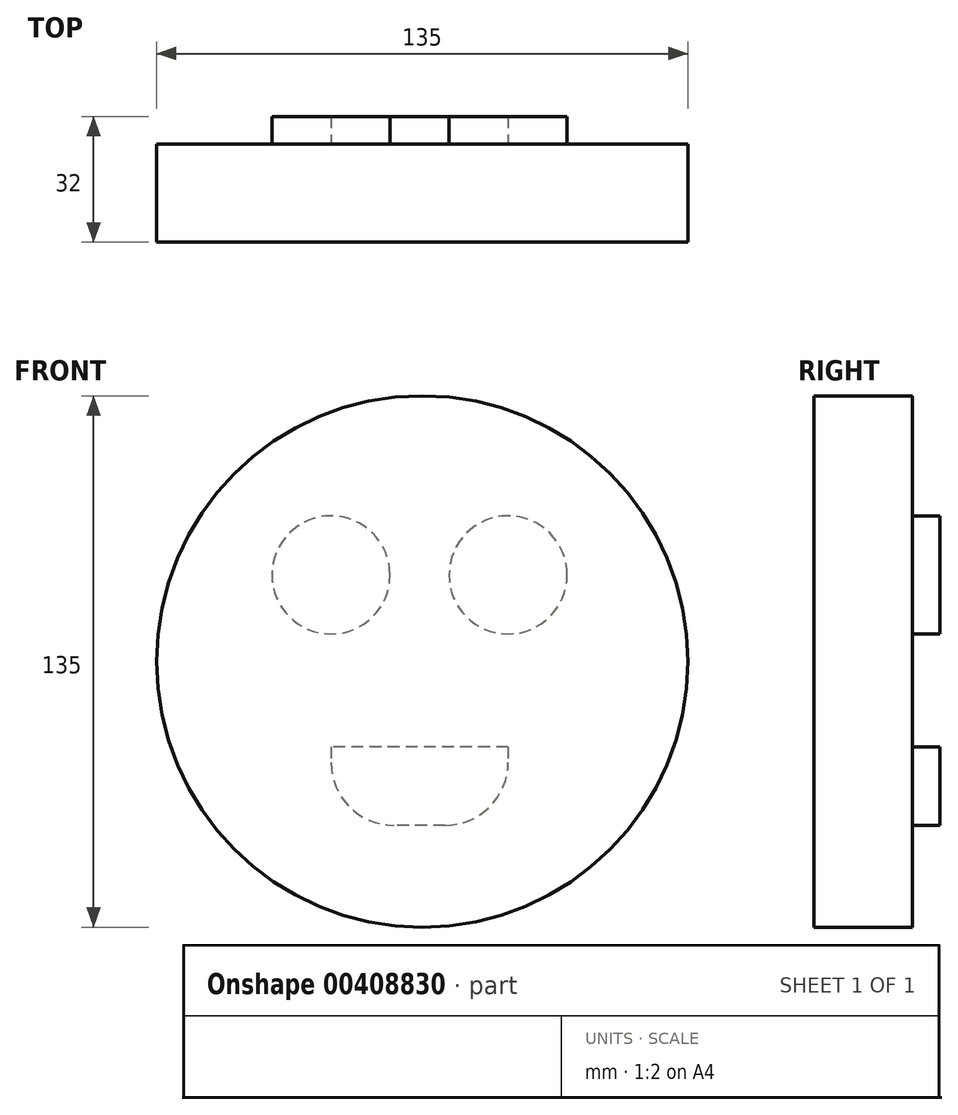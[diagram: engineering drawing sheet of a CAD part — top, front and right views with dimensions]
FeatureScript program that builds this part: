
annotation { "Feature Type Name" : "Feature", "Feature Type Description" : "" }
export const myFeature = defineFeature(function(context is Context, id is Id, definition is map)
    precondition{}
    {
        {
            var Q0;
            Q0=qCreatedBy(makeId("Front.planeOp"),FACE);
            var sketch = newSketch(context, id + "F0", { "sketchPlane" : qUnion([Q0])});
            skCircle(sketch, "E0", {"center": v(0, 0) * mm, "radius": 67.5 * mm});
            skSolve(sketch);
        }
        {
            var Q0;
            Q0 = qSketchRegion(id + "F0", true);
            extrude(context, id + "F1", {"entities" : qUnion([Q0]), "depth" : 25 * mm});
        }
        {
            var Q0;
            Q0=qCreatedBy(makeId("Front.planeOp"),FACE);
            var sketch = newSketch(context, id + "F2", { "sketchPlane" : qUnion([Q0])});
            skCircle(sketch, "E1", {"center": v(-23.18, 22) * mm, "radius": 15 * mm});
            skCircle(sketch, "E2", {"center": v(21.82, 22) * mm, "radius": 15 * mm});
            skLineSegment(sketch, "E3.bottom", {"start": v(21.82, -21.7) * mm, "end": v(-23.18, -21.7) * mm});
            skLineSegment(sketch, "E3.top", {"start": v(21.82, -41.6) * mm, "end": v(-23.18, -41.6) * mm});
            skLineSegment(sketch, "E3.left", {"start": v(21.82, -21.7) * mm, "end": v(21.82, -41.6) * mm});
            skLineSegment(sketch, "E3.right", {"start": v(-23.18, -21.7) * mm, "end": v(-23.18, -41.6) * mm});
            skSolve(sketch);
        }
        {
            var Q0;
            Q0 = qSketchRegion(id + "F2", true);
            extrude(context, id + "F3", {"entities" : qUnion([Q0]), "operationType" : NewBodyOperationType.ADD, "oppositeDirection" : true, "depth" : 7 * mm});
        }
        {
            var Q0;
            Q0=makeQuery(id+"F3.opExtrude","SWEPT_EDGE",EDGE,{"disambiguationData":[OSD([sQuery(id+"F2.wireOp",EDGE,"E3.top"),sQuery(id+"F2.wireOp",EDGE,"E3.left")])]});
            var Q1;
            Q1=makeQuery(id+"F3.opExtrude","SWEPT_EDGE",EDGE,{"disambiguationData":[OSD([sQuery(id+"F2.wireOp",EDGE,"E3.top"),sQuery(id+"F2.wireOp",EDGE,"E3.right")])]});
            fillet(context, id + "F4", {"entities" : qUnion([Q0, Q1]), "radius" : 16 * mm, "tangentPropagation" : true, "allowEdgeOverflow" : false});
        }
    });
